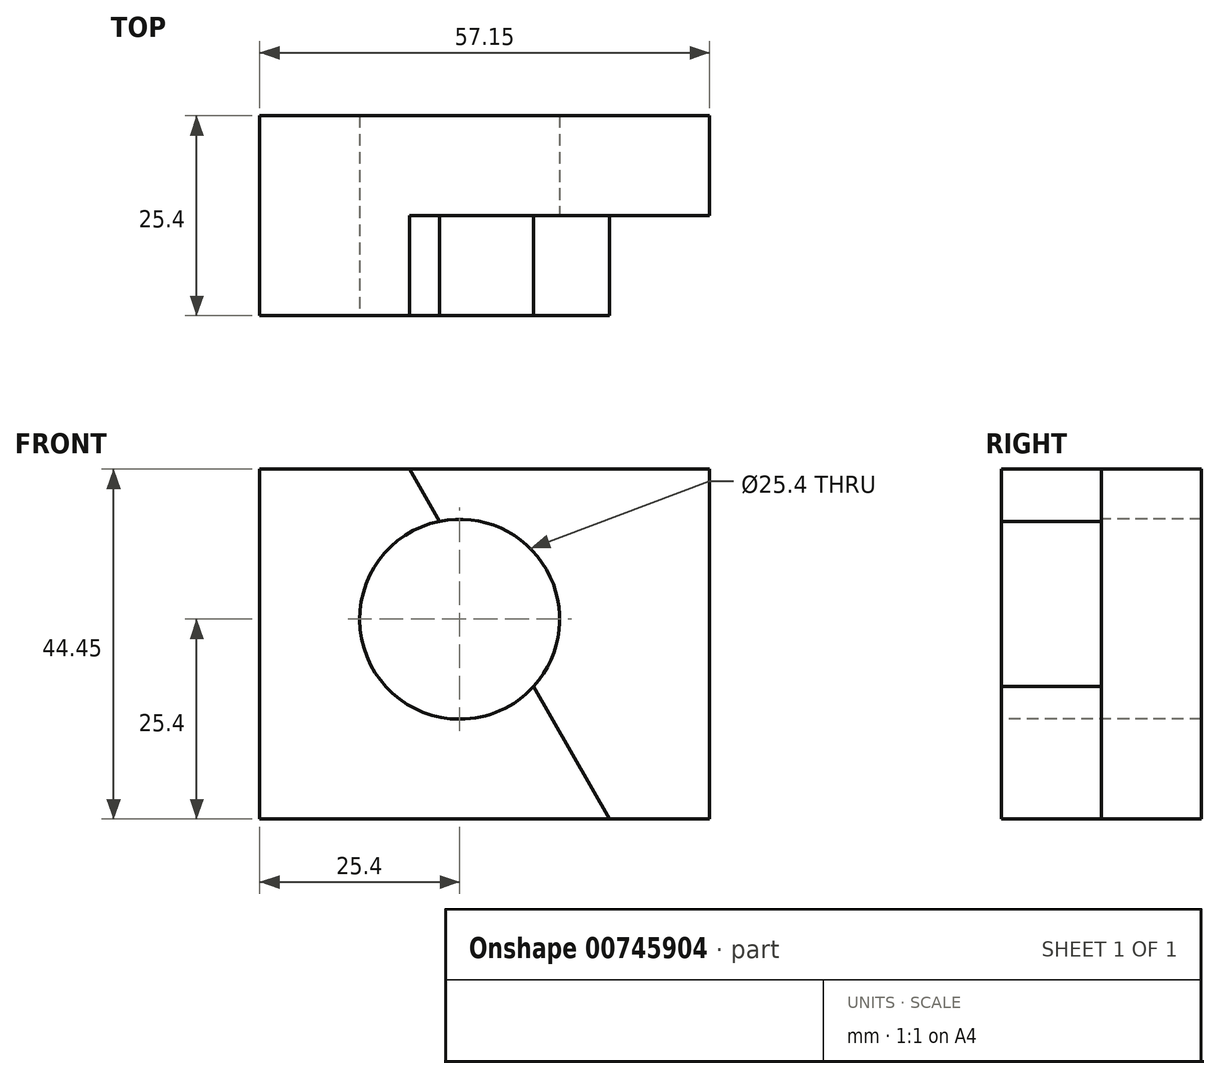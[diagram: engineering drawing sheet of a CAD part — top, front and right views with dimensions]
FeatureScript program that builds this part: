
annotation { "Feature Type Name" : "Feature", "Feature Type Description" : "" }
export const myFeature = defineFeature(function(context is Context, id is Id, definition is map)
    precondition{}
    {
        {
            var Q0;
            Q0=qCreatedBy(makeId("Front.planeOp"),FACE);
            var sketch = newSketch(context, id + "F0", { "sketchPlane" : qUnion([Q0])});
            skLineSegment(sketch, "E0.bottom", {"start": v(0, 0) * mm, "end": v(57.15, 0) * mm});
            skLineSegment(sketch, "E0.top", {"start": v(0, 44.45) * mm, "end": v(57.15, 44.45) * mm});
            skLineSegment(sketch, "E0.left", {"start": v(0, 0) * mm, "end": v(0, 44.45) * mm});
            skLineSegment(sketch, "E0.right", {"start": v(57.15, 0) * mm, "end": v(57.15, 44.45) * mm});
            skSolve(sketch);
        }
        {
            var Q0;
            Q0=makeQuery(id+"F0.imprint","IMPRINT",FACE,{"disambiguationData":[TD([[makeQuery(id+"F0.imprint","IMPRINT",EDGE,{"derivedFrom":sQuery(id+"F0.wireOp",EDGE,"E0.bottom")}),1.0]])]});
            extrude(context, id + "F1", {"entities" : qUnion([Q0]), "oppositeDirection" : true, "depth" : 25.4 * mm, "offsetDistance" : 25.4 * mm});
        }
        {
            var Q0;
            Q0=makeQuery(id+"F1.opExtrude","CAP_FACE",FACE,{"disambiguationData":[OSD([sQuery(id+"F0.wireOp",EDGE,"E0.bottom"),sQuery(id+"F0.wireOp",EDGE,"E0.top"),sQuery(id+"F0.wireOp",EDGE,"E0.left"),sQuery(id+"F0.wireOp",EDGE,"E0.right")])],"isStart":true});
            var sketch = newSketch(context, id + "F2", { "sketchPlane" : qUnion([Q0])});
            skLineSegment(sketch, "E1", {"start": v(19.05, 44.45) * mm, "end": v(44.45, 0) * mm});
            skSolve(sketch);
        }
        {
            var Q0;
            {var subQ0=sQuery(id+"F2.wireOp",EDGE,"E1");Q0=makeQuery(id+"F2.imprint","IMPRINT",FACE,{"disambiguationData":[TD([[makeQuery(id+"F2.imprint","IMPRINT",EDGE,{"derivedFrom":subQ0}),1.0]])]});}
            extrude(context, id + "F3", {"entities" : qUnion([Q0]), "operationType" : NewBodyOperationType.REMOVE, "oppositeDirection" : true, "depth" : 12.7 * mm, "offsetDistance" : 25.4 * mm});
        }
        {
            var Q0;
            Q0=makeQuery(id+"F1.opExtrude","CAP_FACE",FACE,{"disambiguationData":[OSD([sQuery(id+"F0.wireOp",EDGE,"E0.bottom"),sQuery(id+"F0.wireOp",EDGE,"E0.top"),sQuery(id+"F0.wireOp",EDGE,"E0.left"),sQuery(id+"F0.wireOp",EDGE,"E0.right")])],"isStart":true});
            var sketch = newSketch(context, id + "F4", { "sketchPlane" : qUnion([Q0])});
            skCircle(sketch, "E2", {"center": v(25.4, 25.4) * mm, "radius": 12.7 * mm});
            skSolve(sketch);
        }
        {
            var Q0;
            {var subQ0=sQuery(id+"F4.wireOp",EDGE,"E2");var subQ1=makeQuery(id+"F3.boolean.opBoolean","COPY",EDGE,{"derivedFrom":makeQuery(id+"F3.opExtrude","CAP_EDGE",EDGE,{"disambiguationData":[OSD([sQuery(id+"F2.wireOp",EDGE,"E1")])],"isStart":true})});var subQ2=makeQuery(id+"F4.imprint","INTERSECT",VERTEX,{"disambiguationData":[OD(0.0)],"derivedFrom":[subQ1,subQ0]});Q0=makeQuery(id+"F4.imprint","IMPRINT",FACE,{"disambiguationData":[TD([[makeQuery(id+"F4.imprint","IMPRINT",EDGE,{"disambiguationData":[TD([[subQ2,1.0]])],"derivedFrom":subQ0}),1.0]])]});}
            var Q1;
            {var subQ0=sQuery(id+"F4.wireOp",EDGE,"E2");var subQ1=makeQuery(id+"F3.boolean.opBoolean","COPY",EDGE,{"derivedFrom":makeQuery(id+"F3.opExtrude","CAP_EDGE",EDGE,{"disambiguationData":[OSD([sQuery(id+"F2.wireOp",EDGE,"E1")])],"isStart":true})});var subQ2=makeQuery(id+"F4.imprint","INTERSECT",VERTEX,{"disambiguationData":[OD(0.0)],"derivedFrom":[subQ1,subQ0]});Q1=makeQuery(id+"F4.imprint","IMPRINT",FACE,{"disambiguationData":[TD([[makeQuery(id+"F4.imprint","IMPRINT",EDGE,{"disambiguationData":[TD([[subQ2,-1.0]])],"derivedFrom":subQ0}),1.0]])]});}
            extrude(context, id + "F5", {"entities" : qUnion([Q0, Q1]), "operationType" : NewBodyOperationType.REMOVE, "oppositeDirection" : true, "depth" : 25.4 * mm, "offsetDistance" : 25.4 * mm});
        }
    });
